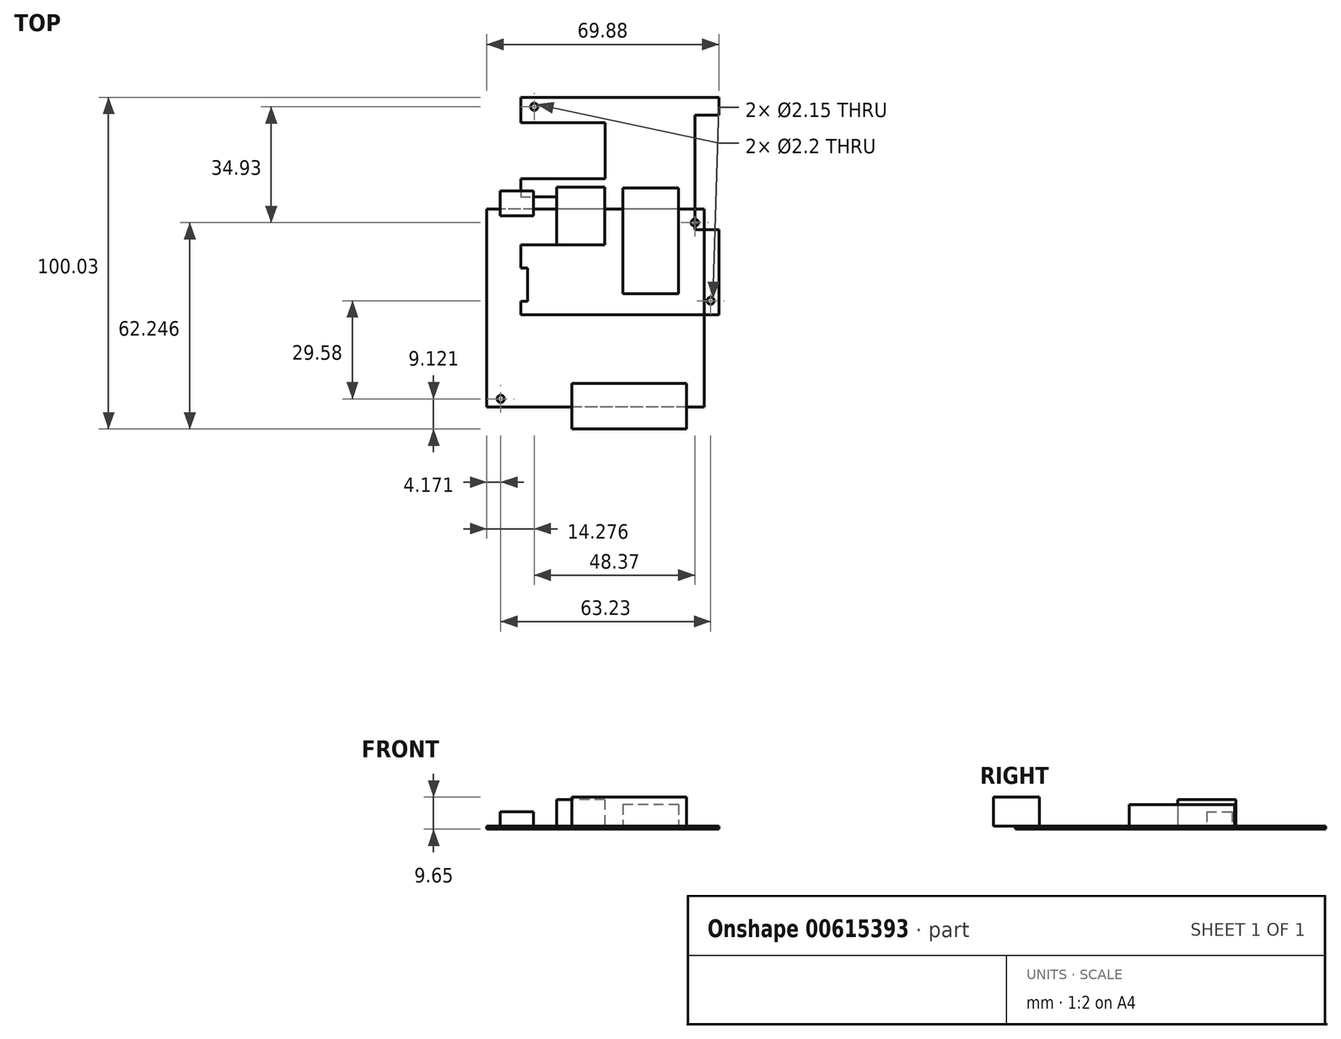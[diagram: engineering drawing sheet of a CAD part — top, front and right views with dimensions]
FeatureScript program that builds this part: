
annotation { "Feature Type Name" : "Feature", "Feature Type Description" : "" }
export const myFeature = defineFeature(function(context is Context, id is Id, definition is map)
    precondition{}
    {
        {
            var Q0;
            Q0=qCreatedBy(makeId("Top.planeOp"),FACE);
            var sketch = newSketch(context, id + "F0", { "sketchPlane" : qUnion([Q0])});
            skLineSegment(sketch, "E0.bottom", {"start": v(-36.01, 49.1) * mm, "end": v(23.69, 49.1) * mm});
            skLineSegment(sketch, "E0.top", {"start": v(-36.01, -16.4) * mm, "end": v(23.69, -16.4) * mm});
            skLineSegment(sketch, "E0.left", {"start": v(-36.01, 49.1) * mm, "end": v(-36.01, -16.4) * mm});
            skLineSegment(sketch, "E0.right", {"start": v(23.69, 49.1) * mm, "end": v(23.69, -16.4) * mm});
            skLineSegment(sketch, "E1.bottom", {"start": v(-42.31, 41.4) * mm, "end": v(-10.51, 41.4) * mm});
            skLineSegment(sketch, "E1.top", {"start": v(-42.31, 24.6) * mm, "end": v(-10.51, 24.6) * mm});
            skLineSegment(sketch, "E1.left", {"start": v(-42.31, 41.4) * mm, "end": v(-42.31, 24.6) * mm});
            skLineSegment(sketch, "E1.right", {"start": v(-10.51, 41.4) * mm, "end": v(-10.51, 24.6) * mm});
            skLineSegment(sketch, "E2.bottom", {"start": v(-33.91, -12.4) * mm, "end": v(-41.51, -12.4) * mm});
            skLineSegment(sketch, "E2.top", {"start": v(-33.91, -2.4) * mm, "end": v(-41.51, -2.4) * mm});
            skLineSegment(sketch, "E2.left", {"start": v(-33.91, -12.4) * mm, "end": v(-33.91, -2.4) * mm});
            skLineSegment(sketch, "E2.right", {"start": v(-41.51, -12.4) * mm, "end": v(-41.51, -2.4) * mm});
            skLineSegment(sketch, "E3.bottom", {"start": v(-42.64, 19.1) * mm, "end": v(-25.2, 19.1) * mm});
            skLineSegment(sketch, "E3.top", {"start": v(-42.64, 4.6) * mm, "end": v(-25.2, 4.6) * mm});
            skLineSegment(sketch, "E3.left", {"start": v(-42.64, 19.1) * mm, "end": v(-42.64, 4.6) * mm});
            skLineSegment(sketch, "E3.right", {"start": v(-25.2, 19.1) * mm, "end": v(-25.2, 4.6) * mm});
            skLineSegment(sketch, "E4.bottom", {"start": v(30.34, 43.7) * mm, "end": v(16.5, 43.7) * mm});
            skLineSegment(sketch, "E4.top", {"start": v(30.34, 9.2) * mm, "end": v(16.5, 9.2) * mm});
            skLineSegment(sketch, "E4.left", {"start": v(30.34, 43.7) * mm, "end": v(30.34, 9.2) * mm});
            skLineSegment(sketch, "E4.right", {"start": v(16.5, 43.7) * mm, "end": v(16.5, 9.2) * mm});
            skCircle(sketch, "E5", {"center": v(-31.91, 46.26) * mm, "radius": 1.1 * mm});
            skCircle(sketch, "E6", {"center": v(21.21, -12.22) * mm, "radius": 1.07 * mm});
            skSolve(sketch);
        }
        {
            var Q0;
            {var subQ5=sQuery(id+"F0.wireOp",EDGE,"E1.left");Q0=makeQuery(id+"F0.imprint","IMPRINT",FACE,{"disambiguationData":[TD([[makeQuery(id+"F0.imprint","IMPRINT",EDGE,{"derivedFrom":subQ5}),1.0]])]});}
            var Q1;
            {var subQ5=sQuery(id+"F0.wireOp",EDGE,"E1.right");Q1=makeQuery(id+"F0.imprint","IMPRINT",FACE,{"disambiguationData":[TD([[makeQuery(id+"F0.imprint","IMPRINT",EDGE,{"derivedFrom":subQ5}),-1.0]])]});}
            extrude(context, id + "F1", {"entities" : qUnion([Q0, Q1]), "depth" : 6.5 * mm, "offsetDistance" : 25 * mm});
        }
        {
            var Q0;
            {var subQ5=sQuery(id+"F0.wireOp",EDGE,"E3.left");Q0=makeQuery(id+"F0.imprint","IMPRINT",FACE,{"disambiguationData":[TD([[makeQuery(id+"F0.imprint","IMPRINT",EDGE,{"derivedFrom":subQ5}),1.0]])]});}
            var Q1;
            {var subQ5=sQuery(id+"F0.wireOp",EDGE,"E3.right");Q1=makeQuery(id+"F0.imprint","IMPRINT",FACE,{"disambiguationData":[TD([[makeQuery(id+"F0.imprint","IMPRINT",EDGE,{"derivedFrom":subQ5}),-1.0]])]});}
            extrude(context, id + "F2", {"entities" : qUnion([Q0, Q1]), "depth" : 8 * mm, "offsetDistance" : 25 * mm});
        }
        {
            var Q0;
            {var subQ5=sQuery(id+"F0.wireOp",EDGE,"E2.left");Q0=makeQuery(id+"F0.imprint","IMPRINT",FACE,{"disambiguationData":[TD([[makeQuery(id+"F0.imprint","IMPRINT",EDGE,{"derivedFrom":subQ5}),1.0]])]});}
            var Q1;
            {var subQ5=sQuery(id+"F0.wireOp",EDGE,"E2.right");Q1=makeQuery(id+"F0.imprint","IMPRINT",FACE,{"disambiguationData":[TD([[makeQuery(id+"F0.imprint","IMPRINT",EDGE,{"derivedFrom":subQ5}),-1.0]])]});}
            extrude(context, id + "F3", {"entities" : qUnion([Q0, Q1]), "depth" : 4.3 * mm, "offsetDistance" : 25 * mm});
        }
        {
            var Q0;
            {var subQ5=sQuery(id+"F0.wireOp",EDGE,"E4.right");Q0=makeQuery(id+"F0.imprint","IMPRINT",FACE,{"disambiguationData":[TD([[makeQuery(id+"F0.imprint","IMPRINT",EDGE,{"derivedFrom":subQ5}),1.0]])]});}
            var Q1;
            {var subQ5=sQuery(id+"F0.wireOp",EDGE,"E4.left");Q1=makeQuery(id+"F0.imprint","IMPRINT",FACE,{"disambiguationData":[TD([[makeQuery(id+"F0.imprint","IMPRINT",EDGE,{"derivedFrom":subQ5}),-1.0]])]});}
            extrude(context, id + "F4", {"entities" : qUnion([Q0, Q1]), "depth" : 8.75 * mm, "offsetDistance" : 25 * mm});
        }
        {
            var Q0;
            {var subQ1=sQuery(id+"F0.wireOp",EDGE,"E0.bottom");Q0=makeQuery(id+"F0.imprint","IMPRINT",FACE,{"disambiguationData":[TD([[makeQuery(id+"F0.imprint","IMPRINT",EDGE,{"derivedFrom":subQ1}),-1.0]])]});}
            var Q1;
            {var subQ5=sQuery(id+"F0.wireOp",EDGE,"E4.right");Q1=makeQuery(id+"F0.imprint","IMPRINT",FACE,{"disambiguationData":[TD([[makeQuery(id+"F0.imprint","IMPRINT",EDGE,{"derivedFrom":subQ5}),1.0]])]});}
            var Q2;
            {var subQ5=sQuery(id+"F0.wireOp",EDGE,"E1.right");Q2=makeQuery(id+"F0.imprint","IMPRINT",FACE,{"disambiguationData":[TD([[makeQuery(id+"F0.imprint","IMPRINT",EDGE,{"derivedFrom":subQ5}),-1.0]])]});}
            var Q3;
            {var subQ5=sQuery(id+"F0.wireOp",EDGE,"E3.right");Q3=makeQuery(id+"F0.imprint","IMPRINT",FACE,{"disambiguationData":[TD([[makeQuery(id+"F0.imprint","IMPRINT",EDGE,{"derivedFrom":subQ5}),-1.0]])]});}
            var Q4;
            {var subQ5=sQuery(id+"F0.wireOp",EDGE,"E2.left");Q4=makeQuery(id+"F0.imprint","IMPRINT",FACE,{"disambiguationData":[TD([[makeQuery(id+"F0.imprint","IMPRINT",EDGE,{"derivedFrom":subQ5}),1.0]])]});}
            extrude(context, id + "F5", {"entities" : qUnion([Q0, Q1, Q2, Q3, Q4]), "oppositeDirection" : true, "depth" : 0.9 * mm, "offsetDistance" : 25 * mm});
        }
        {
            var Q0;
            Q0=makeQuery(id+"F1.opExtrude","SWEPT_BODY",BODY,{"disambiguationData":[OSD([sQuery(id+"F0.wireOp",EDGE,"E1.bottom"),sQuery(id+"F0.wireOp",EDGE,"E1.top"),sQuery(id+"F0.wireOp",EDGE,"E1.left"),sQuery(id+"F0.wireOp",EDGE,"E1.right")])]});
            var Q1;
            Q1=makeQuery(id+"F2.opExtrude","SWEPT_BODY",BODY,{"disambiguationData":[OSD([sQuery(id+"F0.wireOp",EDGE,"E3.bottom"),sQuery(id+"F0.wireOp",EDGE,"E3.top"),sQuery(id+"F0.wireOp",EDGE,"E3.left"),sQuery(id+"F0.wireOp",EDGE,"E3.right")])]});
            var Q2;
            Q2=makeQuery(id+"F4.opExtrude","SWEPT_BODY",BODY,{"disambiguationData":[OSD([sQuery(id+"F0.wireOp",EDGE,"E4.bottom"),sQuery(id+"F0.wireOp",EDGE,"E4.top"),sQuery(id+"F0.wireOp",EDGE,"E4.left"),sQuery(id+"F0.wireOp",EDGE,"E4.right")])]});
            var Q3;
            Q3=makeQuery(id+"F5.opExtrude","SWEPT_BODY",BODY,{"disambiguationData":[OSD([sQuery(id+"F0.wireOp",EDGE,"E0.bottom"),sQuery(id+"F0.wireOp",EDGE,"E0.top"),sQuery(id+"F0.wireOp",EDGE,"E0.left"),sQuery(id+"F0.wireOp",EDGE,"E0.right"),sQuery(id+"F0.wireOp",EDGE,"E5"),sQuery(id+"F0.wireOp",EDGE,"E6")])]});
            var Q4;
            Q4=makeQuery(id+"F3.opExtrude","SWEPT_BODY",BODY,{"disambiguationData":[OSD([sQuery(id+"F0.wireOp",EDGE,"E2.bottom"),sQuery(id+"F0.wireOp",EDGE,"E2.top"),sQuery(id+"F0.wireOp",EDGE,"E2.left"),sQuery(id+"F0.wireOp",EDGE,"E2.right")])]});
            var Q5;
            Q5=makeQuery(id+"F2.opExtrude","SWEPT_EDGE",EDGE,{"disambiguationData":[OSD([sQuery(id+"F0.wireOp",EDGE,"E3.top"),sQuery(id+"F0.wireOp",EDGE,"E3.right")])]});
            transform(context, id + "F6", {"entities" : qUnion([Q0, Q1, Q2, Q3, Q4]), "transformType" : TransformType.ROTATION, "transformAxis" : qUnion([Q5]), "angle" : 90 * degree, "makeCopy" : false});
        }
        {
            var Q0;
            {var subQ1=sQuery(id+"F0.wireOp",EDGE,"E0.bottom");Q0=makeQuery(id+"F0.imprint","IMPRINT",FACE,{"disambiguationData":[TD([[makeQuery(id+"F0.imprint","IMPRINT",EDGE,{"derivedFrom":subQ1}),-1.0]])]});}
            extrude(context, id + "F7", {"entities" : qUnion([Q0]), "oppositeDirection" : true, "depth" : 0.9 * mm, "offsetDistance" : 25 * mm});
        }
    });
